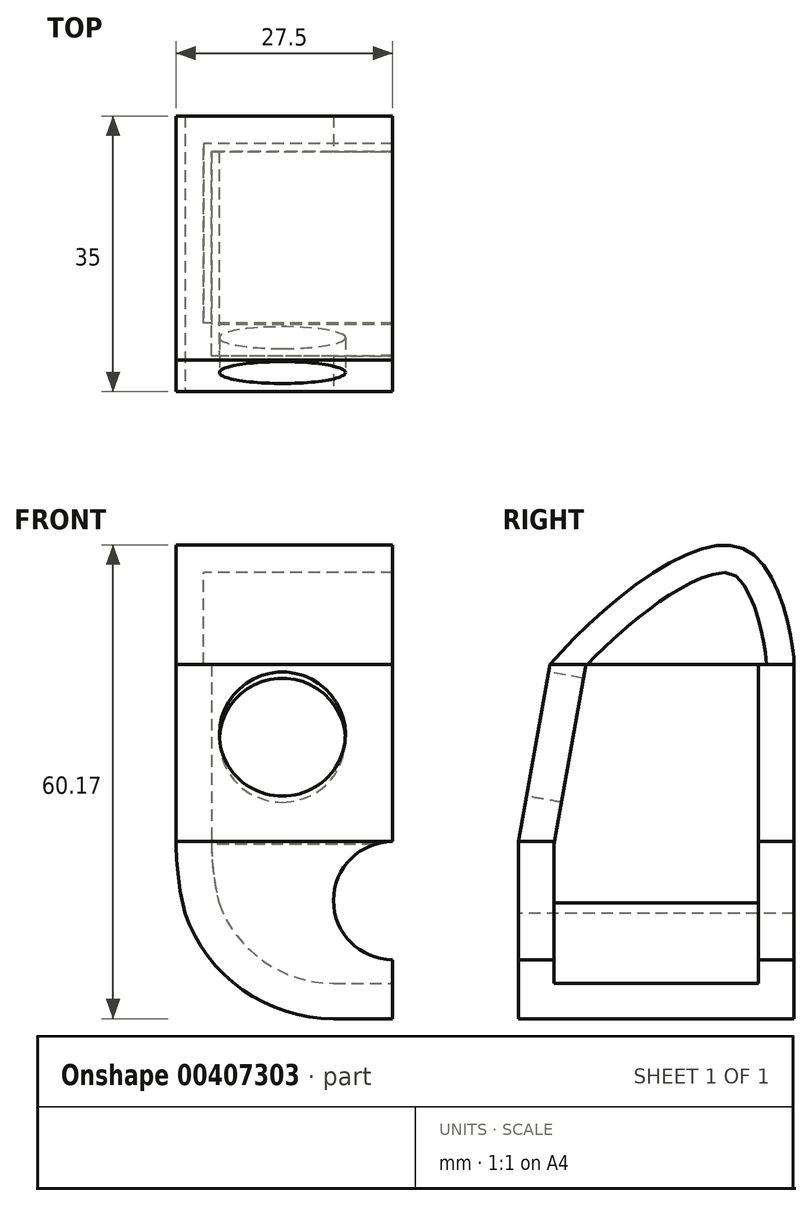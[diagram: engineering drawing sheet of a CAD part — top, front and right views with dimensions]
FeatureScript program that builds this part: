
annotation { "Feature Type Name" : "Feature", "Feature Type Description" : "" }
export const myFeature = defineFeature(function(context is Context, id is Id, definition is map)
    precondition{}
    {
        {
            var Q0;
            Q0=qCreatedBy(makeId("Top.planeOp"),FACE);
            var sketch = newSketch(context, id + "F0", { "sketchPlane" : qUnion([Q0])});
            skLineSegment(sketch, "E0.bottom", {"start": v(0, 0) * mm, "end": v(27.5, 0) * mm});
            skLineSegment(sketch, "E0.top", {"start": v(0, -35) * mm, "end": v(27.5, -35) * mm});
            skLineSegment(sketch, "E0.left", {"start": v(0, 0) * mm, "end": v(0, -35) * mm});
            skLineSegment(sketch, "E0.right", {"start": v(27.5, 0) * mm, "end": v(27.5, -35) * mm});
            skSolve(sketch);
        }
        {
            var Q0;
            Q0 = qSketchRegion(id + "F0", true);
            extrude(context, id + "F1", {"entities" : qUnion([Q0]), "depth" : 45 * mm});
        }
        {
            var Q0;
            Q0=makeQuery(id+"F1.opExtrude","SWEPT_FACE",FACE,{"disambiguationData":[OSD([sQuery(id+"F0.wireOp",EDGE,"E0.top")])]});
            var sketch = newSketch(context, id + "F2", { "sketchPlane" : qUnion([Q0])});
            skLineSegment(sketch, "E1", {"start": v(27.5, 0) * mm, "end": v(27.5, 15) * mm});
            skCircle(sketch, "E2", {"center": v(27.5, 15) * mm, "radius": 7.5 * mm});
            skLineSegment(sketch, "E3", {"start": v(27.5, 0) * mm, "end": v(7.5, 0) * mm});
            skLineSegment(sketch, "E4", {"start": v(7.5, 0) * mm, "end": v(7.5, 22.5) * mm});
            skLineSegment(sketch, "E5", {"start": v(7.5, 22.5) * mm, "end": v(0, 22.5) * mm});
            skLineSegment(sketch, "E6", {"start": v(0, 22.5) * mm, "end": v(0, 0) * mm});
            skLineSegment(sketch, "E7", {"start": v(0, 0) * mm, "end": v(7.5, 0) * mm});
            skArc(sketch, "E8", {"start": v(0, 22.5) * mm, "mid": v(1.92, 10.64) * mm, "end": v(7.5, 0) * mm});
            skSolve(sketch);
        }
        {
            var Q0;
            Q0=makeQuery(id+"F1.opExtrude","CAP_EDGE",EDGE,{"disambiguationData":[OSD([sQuery(id+"F0.wireOp",EDGE,"E0.left")])],"isStart":true});
            fillet(context, id + "F3", {"entities" : qUnion([Q0]), "radius" : 20 * mm, "tangentPropagation" : true, "allowEdgeOverflow" : false});
        }
        {
            var Q0;
            Q0=makeQuery(id+"F2.imprint","IMPRINT",FACE,{"disambiguationData":[TD([[makeQuery(id+"F2.imprint","IMPRINT",EDGE,{"derivedFrom":sQuery(id+"F2.wireOp",EDGE,"E6")}),1.0]])]});
            var Q1;
            {var subQ0=sQuery(id+"F2.wireOp",EDGE,"E1");var subQ3=sQuery(id+"F2.wireOp",EDGE,"E2");var subQ4=makeQuery(id+"F2.imprint","INTERSECT",VERTEX,{"derivedFrom":[subQ0,subQ3]});Q1=makeQuery(id+"F2.imprint","IMPRINT",FACE,{"disambiguationData":[TD([[makeQuery(id+"F2.imprint","IMPRINT",EDGE,{"disambiguationData":[TD([[subQ4,1.0]])],"derivedFrom":subQ0}),-1.0]])]});}
            extrude(context, id + "F4", {"entities" : qUnion([Q0, Q1]), "operationType" : NewBodyOperationType.REMOVE, "oppositeDirection" : true, "depth" : 35 * mm});
        }
        {
            var Q0;
            Q0=makeQuery(id+"F1.opExtrude","SWEPT_FACE",FACE,{"disambiguationData":[OSD([sQuery(id+"F0.wireOp",EDGE,"E0.left")])]});
            var sketch = newSketch(context, id + "F5", { "sketchPlane" : qUnion([Q0])});
            skLineSegment(sketch, "E9", {"start": v(35, 22.5) * mm, "end": v(31.03, 45) * mm});
            skLineSegment(sketch, "E10", {"start": v(31.03, 45) * mm, "end": v(35, 45) * mm});
            skLineSegment(sketch, "E11", {"start": v(35, 45) * mm, "end": v(35, 22.5) * mm});
            skSolve(sketch);
        }
        {
            var Q0;
            Q0=makeQuery(id+"F5.imprint","IMPRINT",FACE,{"disambiguationData":[TD([[makeQuery(id+"F5.imprint","IMPRINT",EDGE,{"derivedFrom":sQuery(id+"F5.wireOp",EDGE,"E9")}),-1.0]])]});
            extrude(context, id + "F6", {"entities" : qUnion([Q0]), "operationType" : NewBodyOperationType.REMOVE, "oppositeDirection" : true, "depth" : 27.5 * mm});
        }
        {
            var Q0;
            {var subQ0=sQuery(id+"F0.wireOp",EDGE,"E0.bottom");var subQ1=sQuery(id+"F0.wireOp",EDGE,"E0.right");var subQ2=sQuery(id+"F0.wireOp",EDGE,"E0.top");Q0=makeQuery(id+"F4.boolean.opBoolean","SPLIT",FACE,{"disambiguationData":[TD([makeQuery(id+"F1.opExtrude","CAP_FACE",FACE,{"disambiguationData":[OSD([subQ0,subQ2,sQuery(id+"F0.wireOp",EDGE,"E0.left"),subQ1])],"isStart":false})])],"derivedFrom":makeQuery(id+"F1.opExtrude","SWEPT_FACE",FACE,{"disambiguationData":[OSD([subQ1])]})});}
            var Q1;
            Q1=makeQuery(id+"F4.boolean.opBoolean","COPY",FACE,{"derivedFrom":makeQuery(id+"F4.opExtrude","SWEPT_FACE",FACE,{"disambiguationData":[OSD([sQuery(id+"F2.wireOp",EDGE,"E2")])]})});
            var Q2;
            {var subQ0=sQuery(id+"F0.wireOp",EDGE,"E0.bottom");var subQ1=sQuery(id+"F0.wireOp",EDGE,"E0.right");var subQ2=sQuery(id+"F0.wireOp",EDGE,"E0.top");Q2=makeQuery(id+"F4.boolean.opBoolean","SPLIT",FACE,{"disambiguationData":[TD([makeQuery(id+"F1.opExtrude","CAP_FACE",FACE,{"disambiguationData":[OSD([subQ0,subQ2,sQuery(id+"F0.wireOp",EDGE,"E0.left"),subQ1])],"isStart":true})])],"derivedFrom":makeQuery(id+"F1.opExtrude","SWEPT_FACE",FACE,{"disambiguationData":[OSD([subQ1])]})});}
            var Q3;
            Q3=makeQuery(id+"F1.opExtrude","CAP_FACE",FACE,{"disambiguationData":[OSD([sQuery(id+"F0.wireOp",EDGE,"E0.bottom"),sQuery(id+"F0.wireOp",EDGE,"E0.top"),sQuery(id+"F0.wireOp",EDGE,"E0.left"),sQuery(id+"F0.wireOp",EDGE,"E0.right")])],"isStart":false});
            shell(context, id + "F7", {"entities" : qUnion([Q0, Q1, Q2, Q3]), "thickness" : 4.5 * mm});
        }
        {
            var Q0;
            Q0=makeQuery(id+"F6.boolean.opBoolean","COPY",FACE,{"derivedFrom":makeQuery(id+"F6.opExtrude","SWEPT_FACE",FACE,{"disambiguationData":[OSD([sQuery(id+"F5.wireOp",EDGE,"E9")])]})});
            var sketch = newSketch(context, id + "F8", { "sketchPlane" : qUnion([Q0])});
            skLineSegment(sketch, "E12", {"start": v(0, -6.56) * mm, "end": v(0, 29.94) * mm});
            skLineSegment(sketch, "E13", {"start": v(0, 29.94) * mm, "end": v(13.5, 29.94) * mm});
            skCircle(sketch, "E14", {"center": v(13.5, 29.94) * mm, "radius": 8 * mm});
            skSolve(sketch);
        }
        {
            var Q0;
            Q0 = qSketchRegion(id + "F8", true);
            extrude(context, id + "F9", {"entities" : qUnion([Q0]), "operationType" : NewBodyOperationType.REMOVE, "oppositeDirection" : true, "depth" : 5 * mm});
        }
        {
            var Q0;
            Q0=makeQuery(id+"F1.opExtrude","SWEPT_FACE",FACE,{"disambiguationData":[OSD([sQuery(id+"F0.wireOp",EDGE,"E0.left")])]});
            var sketch = newSketch(context, id + "F10", { "sketchPlane" : qUnion([Q0])});
            skFitSpline(sketch, "E15.MirrorCS", {"points": [v(31.03, 45) * mm, v(6.17, 59.6) * mm, v(0, 45) * mm, v(0.07, 44.42) * mm, v(1.24, 45) * mm], "startDerivative": vector(-37.18, 42.57) * mm, "endDerivative": vector(34.98, 25.44) * mm});
            skSolve(sketch);
        }
        {
            var Q0;
            Q0 = qSketchRegion(id + "F10", true);
            var Q1;
            {var subQ0=sQuery(id+"F10.wireOp",EDGE,"E15.MirrorCS");var subQ1=makeQuery(id+"F1.opExtrude","CAP_EDGE",EDGE,{"disambiguationData":[OSD([sQuery(id+"F0.wireOp",EDGE,"E0.left")])],"isStart":false});var subQ2=makeQuery(id+"F10.imprint","INTERSECT",VERTEX,{"disambiguationData":[OD(0.0)],"derivedFrom":[subQ1,subQ0]});Q1=makeQuery(id+"F10.imprint","IMPRINT",FACE,{"disambiguationData":[TD([[makeQuery(id+"F10.imprint","IMPRINT",EDGE,{"disambiguationData":[TD([[subQ2,-1.0]])],"derivedFrom":subQ1}),1.0]])]});}
            extrude(context, id + "F11", {"entities" : qUnion([Q0, Q1]), "oppositeDirection" : true, "depth" : 27.5 * mm});
        }
        {
            var Q0;
            Q0=makeQuery(id+"F11.opExtrude","SWEPT_FACE",FACE,{"disambiguationData":[OSD([sQuery(id+"F0.wireOp",EDGE,"E0.left")])]});
            var Q1;
            Q1=makeQuery(id+"F11.opExtrude","CAP_FACE",FACE,{"disambiguationData":[OSD([sQuery(id+"F0.wireOp",EDGE,"E0.left"),sQuery(id+"F10.wireOp",EDGE,"E15.MirrorCS")])],"isStart":false});
            shell(context, id + "F12", {"entities" : qUnion([Q0, Q1]), "thickness" : 3.5 * mm});
        }
    });
